FCSTD DOCUMENT  (FreeCAD 0.19R24291 (Git))
Label: makerbeam_profile_10x10_esquisse
License: All rights reserved
LicenseURL: http://en.wikipedia.org/wiki/All_rights_reserved
objects: Sketcher::SketchObject×1, PartDesign::Body×1
note: 2 computed .brp shape members not serialized (recipe doc carries the construction recipe); baked Part::Feature solids carry a one-line shape summary decoded from their .brp

FEATURE [Sketcher::SketchObject] Sketch
  FullyConstrained = false
  sketch-geometry (73):
    g0: LineSegment StartX=5 StartY=4.8 StartZ=0 EndX=5 EndY=1.7 EndZ=0
    g1: ArcOfCircle CenterX=4.8 CenterY=4.8 CenterZ=0 NormalX=0 NormalY=0 NormalZ=1 AngleXU=1.5708 Radius=0.2 StartAngle=4.71239 EndAngle=6.28319
    g2: LineSegment StartX=1.7 StartY=5 StartZ=0 EndX=4.8 EndY=5 EndZ=0
    g3: ArcOfCircle CenterX=1.7 CenterY=4.8 CenterZ=0 NormalX=0 NormalY=0 NormalZ=1 AngleXU=-3.14159 Radius=0.2 StartAngle=4.71239 EndAngle=6.28319
    g4: LineSegment StartX=1.5 StartY=4.2 StartZ=0 EndX=1.5 EndY=4.8 EndZ=0
    g5: ArcOfCircle CenterX=1.7 CenterY=4.2 CenterZ=0 NormalX=0 NormalY=0 NormalZ=1 AngleXU=-1.5708 Radius=0.2 StartAngle=4.71239 EndAngle=6.28319
    g6: LineSegment StartX=2.75934 StartY=4 StartZ=0 EndX=1.7 EndY=4 EndZ=0
    g7: ArcOfCircle CenterX=2.75934 CenterY=3.8 CenterZ=0 NormalX=0 NormalY=0 NormalZ=1 AngleXU=-1.5708 Radius=0.2 StartAngle=0.717276 EndAngle=3.14159
    g8: LineSegment StartX=1.0565 StartY=2.04928 StartZ=0 EndX=2.89081 EndY=3.64928 EndZ=0
    g9: ArcOfCircle CenterX=0.92503 CenterY=2.2 CenterZ=0 NormalX=0 NormalY=0 NormalZ=1 AngleXU=2.28807 Radius=0.2 StartAngle=2.42432 EndAngle=3.14159
    g10: LineSegment StartX=-0.92503 StartY=2 StartZ=0 EndX=0.92503 EndY=2 EndZ=0
    g11: ArcOfCircle CenterX=-0.92503 CenterY=2.2 CenterZ=0 NormalX=0 NormalY=0 NormalZ=1 AngleXU=1.5708 Radius=0.2 StartAngle=2.42432 EndAngle=3.14159
    g12: LineSegment StartX=-2.89081 StartY=3.64928 StartZ=0 EndX=-1.0565 EndY=2.04928 EndZ=0
    g13: ArcOfCircle CenterX=-2.75934 CenterY=3.8 CenterZ=0 NormalX=0 NormalY=0 NormalZ=1 AngleXU=0.85352 Radius=0.2 StartAngle=0.717276 EndAngle=3.14159
    g14: LineSegment StartX=-1.7 StartY=4 StartZ=0 EndX=-2.75934 EndY=4 EndZ=0
    g15: ArcOfCircle CenterX=-1.7 CenterY=4.2 CenterZ=0 NormalX=0 NormalY=0 NormalZ=1 AngleXU=0 Radius=0.2 StartAngle=4.71239 EndAngle=6.28319
    g16: LineSegment StartX=-1.5 StartY=4.8 StartZ=0 EndX=-1.5 EndY=4.2 EndZ=0
    g17: ArcOfCircle CenterX=-1.7 CenterY=4.8 CenterZ=0 NormalX=0 NormalY=0 NormalZ=1 AngleXU=1.5708 Radius=0.2 StartAngle=4.71239 EndAngle=6.28319
    g18: LineSegment StartX=-4.8 StartY=5 StartZ=0 EndX=-1.7 EndY=5 EndZ=0
    g19: ArcOfCircle CenterX=-4.8 CenterY=4.8 CenterZ=0 NormalX=0 NormalY=0 NormalZ=1 AngleXU=-3.14159 Radius=0.2 StartAngle=4.71239 EndAngle=6.28319
    g20: LineSegment StartX=-5 StartY=1.7 StartZ=0 EndX=-5 EndY=4.8 EndZ=0
    g21: ArcOfCircle CenterX=-4.8 CenterY=1.7 CenterZ=0 NormalX=0 NormalY=0 NormalZ=1 AngleXU=-1.5708 Radius=0.2 StartAngle=4.71239 EndAngle=6.28319
    g22: LineSegment StartX=-4.2 StartY=1.5 StartZ=0 EndX=-4.8 EndY=1.5 EndZ=0
    g23: ArcOfCircle CenterX=-4.2 CenterY=1.7 CenterZ=0 NormalX=0 NormalY=0 NormalZ=1 AngleXU=0 Radius=0.2 StartAngle=4.71239 EndAngle=6.28319
    g24: LineSegment StartX=-4 StartY=2.75934 StartZ=0 EndX=-4 EndY=1.7 EndZ=0
    g25: ArcOfCircle CenterX=-3.8 CenterY=2.75934 CenterZ=0 NormalX=0 NormalY=0 NormalZ=1 AngleXU=0 Radius=0.2 StartAngle=0.717276 EndAngle=3.14159
    g26: LineSegment StartX=-2.04928 StartY=1.0565 StartZ=0 EndX=-3.64928 EndY=2.89081 EndZ=0
    g27: ArcOfCircle CenterX=-2.2 CenterY=0.92503 CenterZ=0 NormalX=0 NormalY=0 NormalZ=1 AngleXU=-2.42432 Radius=0.2 StartAngle=2.42432 EndAngle=3.14159
    g28: LineSegment StartX=-2 StartY=-0.92503 StartZ=0 EndX=-2 EndY=0.92503 EndZ=0
    g29: ArcOfCircle CenterX=-2.2 CenterY=-0.92503 CenterZ=0 NormalX=0 NormalY=0 NormalZ=1 AngleXU=-3.14159 Radius=0.2 StartAngle=2.42432 EndAngle=3.14159
    g30: LineSegment StartX=-3.64928 StartY=-2.89081 StartZ=0 EndX=-2.04928 EndY=-1.0565 EndZ=0
    g31: ArcOfCircle CenterX=-3.8 CenterY=-2.75934 CenterZ=0 NormalX=0 NormalY=0 NormalZ=1 AngleXU=2.42432 Radius=0.2 StartAngle=0.717276 EndAngle=3.14159
    g32: LineSegment StartX=-4 StartY=-1.7 StartZ=0 EndX=-4 EndY=-2.75934 EndZ=0
    g33: ArcOfCircle CenterX=-4.2 CenterY=-1.7 CenterZ=0 NormalX=0 NormalY=0 NormalZ=1 AngleXU=1.5708 Radius=0.2 StartAngle=4.71239 EndAngle=6.28319
    g34: LineSegment StartX=-4.8 StartY=-1.5 StartZ=0 EndX=-4.2 EndY=-1.5 EndZ=0
    g35: ArcOfCircle CenterX=-4.8 CenterY=-1.7 CenterZ=0 NormalX=0 NormalY=0 NormalZ=1 AngleXU=-3.14159 Radius=0.2 StartAngle=4.71239 EndAngle=6.28319
    g36: LineSegment StartX=-5 StartY=-4.8 StartZ=0 EndX=-5 EndY=-1.7 EndZ=0
    g37: ArcOfCircle CenterX=-4.8 CenterY=-4.8 CenterZ=0 NormalX=0 NormalY=0 NormalZ=1 AngleXU=-1.5708 Radius=0.2 StartAngle=4.71239 EndAngle=6.28319
    g38: LineSegment StartX=-1.7 StartY=-5 StartZ=0 EndX=-4.8 EndY=-5 EndZ=0
    g39: ArcOfCircle CenterX=-1.7 CenterY=-4.8 CenterZ=0 NormalX=0 NormalY=0 NormalZ=1 AngleXU=0 Radius=0.2 StartAngle=4.71239 EndAngle=6.28319
    g40: LineSegment StartX=-1.5 StartY=-4.2 StartZ=0 EndX=-1.5 EndY=-4.8 EndZ=0
    g41: ArcOfCircle CenterX=-1.7 CenterY=-4.2 CenterZ=0 NormalX=0 NormalY=0 NormalZ=1 AngleXU=1.5708 Radius=0.2 StartAngle=4.71239 EndAngle=6.28319
    g42: LineSegment StartX=-2.75934 StartY=-4 StartZ=0 EndX=-1.7 EndY=-4 EndZ=0
    g43: ArcOfCircle CenterX=-2.75934 CenterY=-3.8 CenterZ=0 NormalX=0 NormalY=0 NormalZ=1 AngleXU=1.5708 Radius=0.2 StartAngle=0.717276 EndAngle=3.14159
    g44: LineSegment StartX=-1.0565 StartY=-2.04928 StartZ=0 EndX=-2.89081 EndY=-3.64928 EndZ=0
    g45: ArcOfCircle CenterX=-0.92503 CenterY=-2.2 CenterZ=0 NormalX=0 NormalY=0 NormalZ=1 AngleXU=-0.85352 Radius=0.2 StartAngle=2.42432 EndAngle=3.14159
    g46: LineSegment StartX=0.92503 StartY=-2 StartZ=0 EndX=-0.92503 EndY=-2 EndZ=0
    g47: ArcOfCircle CenterX=0.92503 CenterY=-2.2 CenterZ=0 NormalX=0 NormalY=0 NormalZ=1 AngleXU=-1.5708 Radius=0.2 StartAngle=2.42432 EndAngle=3.14159
    g48: LineSegment StartX=2.89081 StartY=-3.64928 StartZ=0 EndX=1.0565 EndY=-2.04928 EndZ=0
    g49: ArcOfCircle CenterX=2.75934 CenterY=-3.8 CenterZ=0 NormalX=0 NormalY=0 NormalZ=1 AngleXU=-2.28807 Radius=0.2 StartAngle=0.717276 EndAngle=3.14159
    g50: LineSegment StartX=1.7 StartY=-4 StartZ=0 EndX=2.75934 EndY=-4 EndZ=0
    g51: ArcOfCircle CenterX=1.7 CenterY=-4.2 CenterZ=0 NormalX=0 NormalY=0 NormalZ=1 AngleXU=-3.14159 Radius=0.2 StartAngle=4.71239 EndAngle=6.28319
    g52: LineSegment StartX=1.5 StartY=-4.8 StartZ=0 EndX=1.5 EndY=-4.2 EndZ=0
    g53: ArcOfCircle CenterX=1.7 CenterY=-4.8 CenterZ=0 NormalX=0 NormalY=0 NormalZ=1 AngleXU=-1.5708 Radius=0.2 StartAngle=4.71239 EndAngle=6.28319
    g54: LineSegment StartX=4.8 StartY=-5 StartZ=0 EndX=1.7 EndY=-5 EndZ=0
    g55: ArcOfCircle CenterX=4.8 CenterY=-4.8 CenterZ=0 NormalX=0 NormalY=0 NormalZ=1 AngleXU=0 Radius=0.2 StartAngle=4.71239 EndAngle=6.28319
    g56: LineSegment StartX=5 StartY=-1.7 StartZ=0 EndX=5 EndY=-4.8 EndZ=0
    g57: ArcOfCircle CenterX=4.8 CenterY=-1.7 CenterZ=0 NormalX=0 NormalY=0 NormalZ=1 AngleXU=1.5708 Radius=0.2 StartAngle=4.71239 EndAngle=6.28319
    g58: LineSegment StartX=4.2 StartY=-1.5 StartZ=0 EndX=4.8 EndY=-1.5 EndZ=0
    g59: ArcOfCircle CenterX=4.2 CenterY=-1.7 CenterZ=0 NormalX=0 NormalY=0 NormalZ=1 AngleXU=-3.14159 Radius=0.2 StartAngle=4.71239 EndAngle=6.28319
    g60: LineSegment StartX=4 StartY=-2.75934 StartZ=0 EndX=4 EndY=-1.7 EndZ=0
    g61: ArcOfCircle CenterX=3.8 CenterY=-2.75934 CenterZ=0 NormalX=0 NormalY=0 NormalZ=1 AngleXU=-3.14159 Radius=0.2 StartAngle=0.717276 EndAngle=3.14159
    g62: LineSegment StartX=2.04928 StartY=-1.0565 StartZ=0 EndX=3.64928 EndY=-2.89081 EndZ=0
    g63: ArcOfCircle CenterX=2.2 CenterY=-0.92503 CenterZ=0 NormalX=0 NormalY=0 NormalZ=1 AngleXU=0.717276 Radius=0.2 StartAngle=2.42432 EndAngle=3.14159
    g64: LineSegment StartX=2 StartY=0.92503 StartZ=0 EndX=2 EndY=-0.92503 EndZ=0
    g65: ArcOfCircle CenterX=2.2 CenterY=0.92503 CenterZ=0 NormalX=0 NormalY=0 NormalZ=1 AngleXU=0 Radius=0.2 StartAngle=2.42432 EndAngle=3.14159
    g66: LineSegment StartX=3.64928 StartY=2.89081 StartZ=0 EndX=2.04928 EndY=1.0565 EndZ=0
    g67: ArcOfCircle CenterX=3.8 CenterY=2.75934 CenterZ=0 NormalX=0 NormalY=0 NormalZ=1 AngleXU=-0.717276 Radius=0.2 StartAngle=0.717276 EndAngle=3.14159
    g68: LineSegment StartX=4 StartY=1.7 StartZ=0 EndX=4 EndY=2.75934 EndZ=0
    g69: ArcOfCircle CenterX=4.2 CenterY=1.7 CenterZ=0 NormalX=0 NormalY=0 NormalZ=1 AngleXU=-1.5708 Radius=0.2 StartAngle=4.71239 EndAngle=6.28319
    g70: LineSegment StartX=4.8 StartY=1.5 StartZ=0 EndX=4.2 EndY=1.5 EndZ=0
    g71: ArcOfCircle CenterX=4.8 CenterY=1.7 CenterZ=0 NormalX=0 NormalY=0 NormalZ=1 AngleXU=0 Radius=0.2 StartAngle=4.71239 EndAngle=6.28319
    g72: Circle CenterX=0 CenterY=0 CenterZ=0 NormalX=0 NormalY=0 NormalZ=1 AngleXU=0 Radius=1.25
  constraints (100):
    c: Vertical(g0)
    c: Coincident(g0,g1)
    c: Coincident(g1,g2)
    c: Horizontal(g2)
    c: Coincident(g2,g3)
    c: Coincident(g3,g4)
    c: Vertical(g4)
    c: Coincident(g4,g5)
    c: Coincident(g5,g6)
    c: Horizontal(g6)
    c: Coincident(g6,g7)
    c: Coincident(g7,g8)
    c: Coincident(g8,g9)
    c: Coincident(g9,g10)
    c: Horizontal(g10)
    c: Coincident(g10,g11)
    c: Coincident(g11,g12)
    c: Coincident(g12,g13)
    c: Coincident(g13,g14)
    c: Horizontal(g14)
    c: Coincident(g14,g15)
    c: Coincident(g15,g16)
    c: Vertical(g16)
    c: Coincident(g16,g17)
    c: Coincident(g17,g18)
    c: Horizontal(g18)
    c: Coincident(g18,g19)
    c: Coincident(g19,g20)
    c: Vertical(g20)
    c: Coincident(g20,g21)
    c: Coincident(g21,g22)
    c: Horizontal(g22)
    c: Coincident(g22,g23)
    c: Coincident(g23,g24)
    c: Vertical(g24)
    c: Coincident(g24,g25)
    c: Coincident(g25,g26)
    c: Coincident(g26,g27)
    c: Coincident(g27,g28)
    c: Vertical(g28)
    c: Coincident(g28,g29)
    c: Coincident(g29,g30)
    c: Coincident(g30,g31)
    c: Coincident(g31,g32)
    c: Vertical(g32)
    c: Coincident(g32,g33)
    c: Coincident(g33,g34)
    c: Horizontal(g34)
    c: Coincident(g34,g35)
    c: Coincident(g35,g36)
    c: Vertical(g36)
    c: Coincident(g36,g37)
    c: Coincident(g37,g38)
    c: Horizontal(g38)
    c: Coincident(g38,g39)
    c: Coincident(g39,g40)
    c: Vertical(g40)
    c: Coincident(g40,g41)
    c: Coincident(g41,g42)
    c: Horizontal(g42)
    c: Coincident(g42,g43)
    c: Coincident(g43,g44)
    c: Coincident(g44,g45)
    c: Coincident(g45,g46)
    c: Horizontal(g46)
    c: Coincident(g46,g47)
    c: Coincident(g47,g48)
    c: Coincident(g48,g49)
    c: Coincident(g49,g50)
    c: Horizontal(g50)
    c: Coincident(g50,g51)
    c: Coincident(g51,g52)
    c: Vertical(g52)
    c: Coincident(g52,g53)
    c: Coincident(g53,g54)
    c: Horizontal(g54)
    c: Coincident(g54,g55)
    c: Coincident(g55,g56)
    c: Vertical(g56)
    c: Coincident(g56,g57)
    c: Coincident(g57,g58)
    c: Horizontal(g58)
    c: Coincident(g58,g59)
    c: Coincident(g59,g60)
    c: Vertical(g60)
    c: Coincident(g60,g61)
    c: Coincident(g61,g62)
    c: Coincident(g62,g63)
    c: Coincident(g63,g64)
    c: Vertical(g64)
    c: Coincident(g64,g65)
    c: Coincident(g65,g66)
    c: Coincident(g66,g67)
    c: Coincident(g67,g68)
    c: Vertical(g68)
    c: Coincident(g68,g69)
    c: Coincident(g69,g70)
    c: Horizontal(g70)
    c: Coincident(g70,g71)
    c: Coincident(g71,g0)
FEATURE [PartDesign::Body] Body  label="Body Makerbeam_10x10 esquisse"
  Group = -> [Sketch]
  Origin = -> Origin
